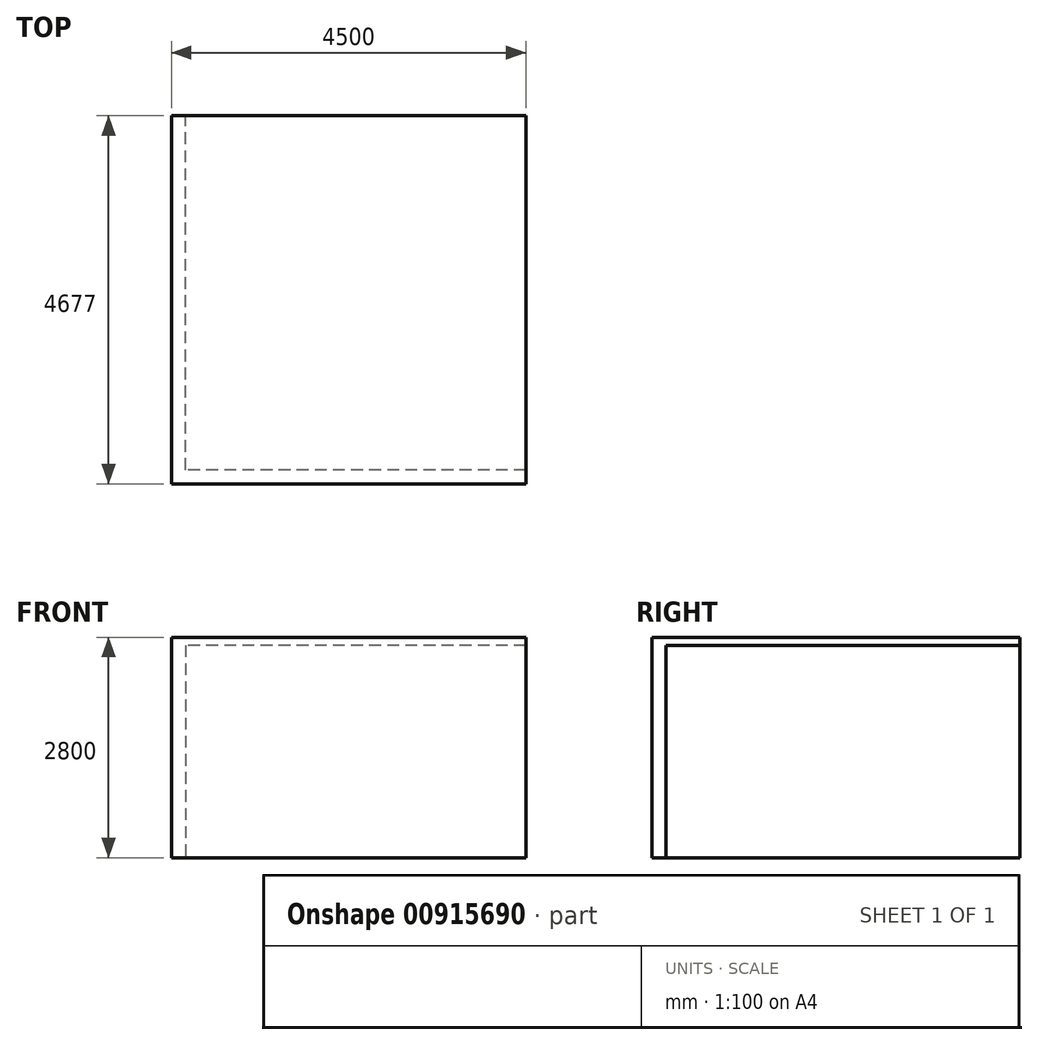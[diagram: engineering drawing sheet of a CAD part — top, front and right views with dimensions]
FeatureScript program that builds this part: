
annotation { "Feature Type Name" : "Feature", "Feature Type Description" : "" }
export const myFeature = defineFeature(function(context is Context, id is Id, definition is map)
    precondition{}
    {
        {
            var Q0;
            Q0=qCreatedBy(makeId("Front.planeOp"),FACE);
            var sketch = newSketch(context, id + "F0", { "sketchPlane" : qUnion([Q0])});
            skLineSegment(sketch, "E0", {"start": v(-102.65, 2725.78) * mm, "end": v(4397.35, 2725.78) * mm});
            skLineSegment(sketch, "E1", {"start": v(4397.35, 2725.78) * mm, "end": v(4397.35, -74.22) * mm});
            skLineSegment(sketch, "E2", {"start": v(4397.35, -74.22) * mm, "end": v(-102.65, -74.22) * mm});
            skLineSegment(sketch, "E3", {"start": v(-102.65, -74.22) * mm, "end": v(-102.65, 2725.78) * mm});
            skSolve(sketch);
        }
        {
            var Q0;
            Q0 = qSketchRegion(id + "F0", true);
            extrude(context, id + "F1", {"entities" : qUnion([Q0]), "oppositeDirection" : true, "depth" : 177 * mm, "offsetDistance" : 25 * mm});
        }
        {
            var Q0;
            Q0=makeQuery(id+"F1.opExtrude","CAP_FACE",FACE,{"disambiguationData":[OSD([sQuery(id+"F0.wireOp",EDGE,"E0"),sQuery(id+"F0.wireOp",EDGE,"E1"),sQuery(id+"F0.wireOp",EDGE,"E2"),sQuery(id+"F0.wireOp",EDGE,"E3")])],"isStart":false});
            var sketch = newSketch(context, id + "F2", { "sketchPlane" : qUnion([Q0])});
            skLineSegment(sketch, "E4.bottom", {"start": v(-72.35, 2725.78) * mm, "end": v(102.65, 2725.78) * mm});
            skLineSegment(sketch, "E4.top", {"start": v(-72.35, -74.22) * mm, "end": v(102.65, -74.22) * mm});
            skLineSegment(sketch, "E4.left", {"start": v(-72.35, 2725.78) * mm, "end": v(-72.35, -74.22) * mm});
            skLineSegment(sketch, "E4.right", {"start": v(102.65, 2725.78) * mm, "end": v(102.65, -74.22) * mm});
            skSolve(sketch);
        }
        {
            var Q0;
            Q0 = qSketchRegion(id + "F2", true);
            extrude(context, id + "F3", {"entities" : qUnion([Q0]), "operationType" : NewBodyOperationType.ADD, "depth" : 4500 * mm, "offsetDistance" : 25 * mm});
        }
        {
            var Q0;
            Q0=makeQuery(id+"F3.boolean.opBoolean","MERGE",FACE,{"derivedFrom":[makeQuery(id+"F1.opExtrude","SWEPT_FACE",FACE,{"disambiguationData":[OSD([sQuery(id+"F0.wireOp",EDGE,"E0")])]}),makeQuery(id+"F3.opExtrude","SWEPT_FACE",FACE,{"disambiguationData":[OSD([sQuery(id+"F2.wireOp",EDGE,"E4.bottom")])]})]});
            var sketch = newSketch(context, id + "F4", { "sketchPlane" : qUnion([Q0])});
            skSolve(sketch);
        }
        {
            var Q0;
            {var subQ1=sQuery(id+"F0.wireOp",EDGE,"E0");Q0=makeQuery(id+"F4.imprint","IMPRINT",FACE,{"disambiguationData":[TD([[makeQuery(id+"F4.imprint","IMPRINT",EDGE,{"derivedFrom":makeQuery(id+"F1.opExtrude","CAP_EDGE",EDGE,{"disambiguationData":[OSD([subQ1])],"isStart":true})}),1.0]])]});}
            var sketch = newSketch(context, id + "F5", { "sketchPlane" : qUnion([Q0])});
            skLineSegment(sketch, "E5.bottom", {"start": v(4397.35, 0) * mm, "end": v(-102.65, 0) * mm});
            skLineSegment(sketch, "E5.top", {"start": v(4397.35, 4677) * mm, "end": v(-102.65, 4677) * mm});
            skLineSegment(sketch, "E5.left", {"start": v(4397.35, 0) * mm, "end": v(4397.35, 4677) * mm});
            skLineSegment(sketch, "E5.right", {"start": v(-102.65, 0) * mm, "end": v(-102.65, 4677) * mm});
            skSolve(sketch);
        }
        {
            var Q0;
            Q0 = qSketchRegion(id + "F5", true);
            extrude(context, id + "F6", {"entities" : qUnion([Q0]), "operationType" : NewBodyOperationType.ADD, "oppositeDirection" : true, "depth" : 100 * mm, "offsetDistance" : 25 * mm});
        }
    });
